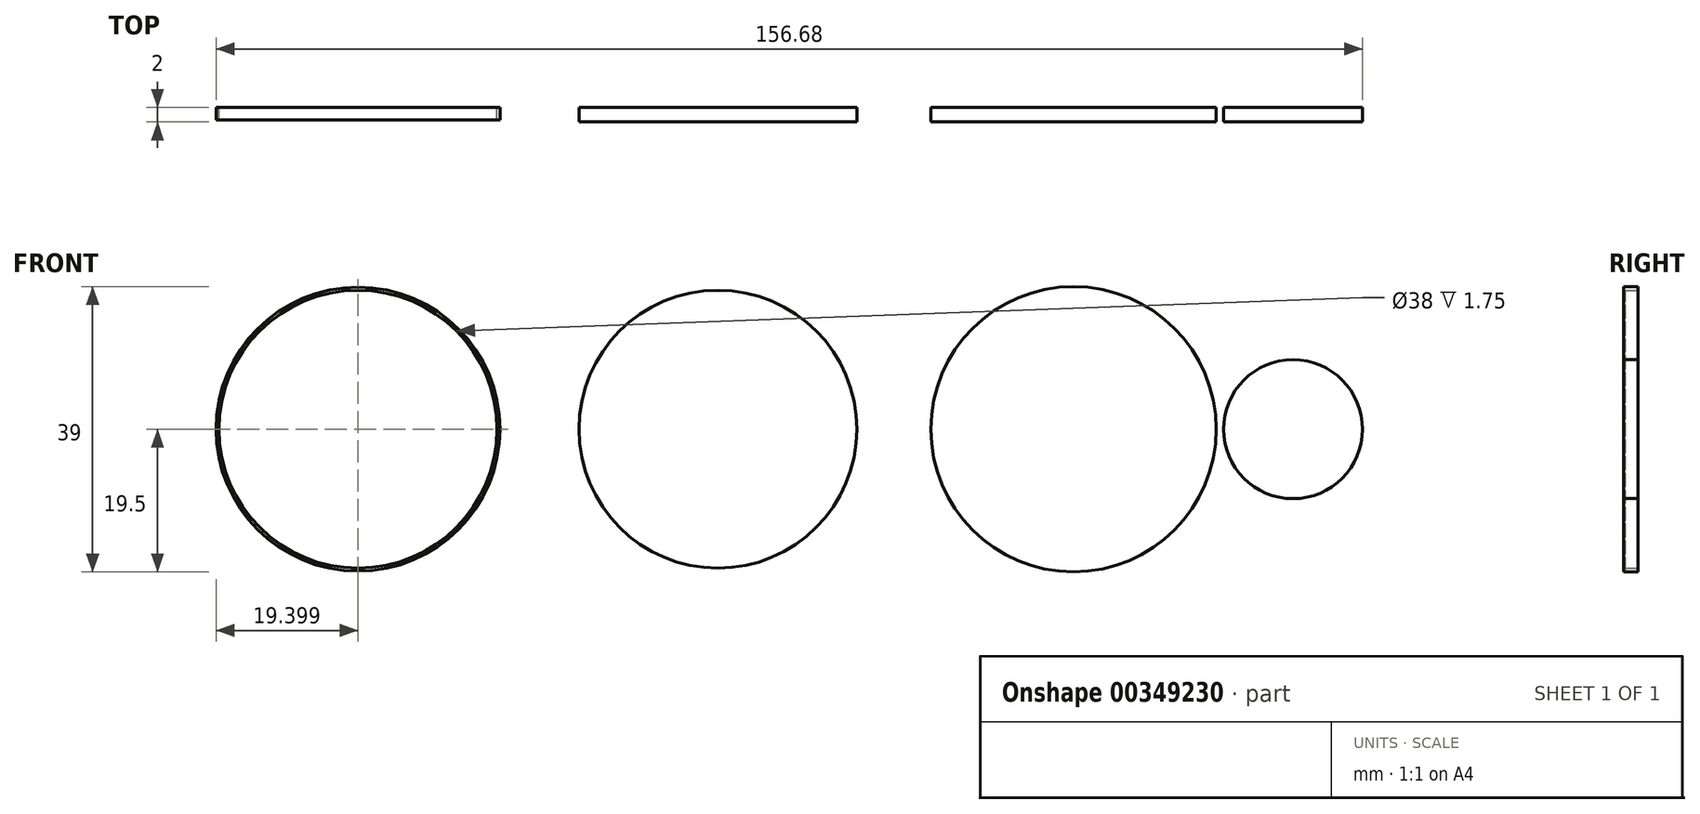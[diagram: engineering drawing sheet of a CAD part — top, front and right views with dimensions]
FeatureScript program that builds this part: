
annotation { "Feature Type Name" : "Feature", "Feature Type Description" : "" }
export const myFeature = defineFeature(function(context is Context, id is Id, definition is map)
    precondition{}
    {
        {
            var Q0;
            Q0=qCreatedBy(makeId("Front.planeOp"),FACE);
            var sketch = newSketch(context, id + "F0", { "sketchPlane" : qUnion([Q0])});
            skCircle(sketch, "E0", {"center": v(0, 0) * mm, "radius": 19.5 * mm});
            skLineSegment(sketch, "E1", {"start": v(0, 0) * mm, "end": v(30, 0) * mm});
            skCircle(sketch, "E2", {"center": v(30, 0) * mm, "radius": 9.5 * mm});
            skCircle(sketch, "E3", {"center": v(-48.6, 0) * mm, "radius": 19 * mm});
            skCircle(sketch, "E4", {"center": v(-97.78, 0) * mm, "radius": 19.4 * mm});
            skCircle(sketch, "E5", {"center": v(-97.78, 0) * mm, "radius": 19 * mm});
            skSolve(sketch);
        }
        {
            var Q0;
            Q0=makeQuery(id+"F0.imprint","IMPRINT",FACE,{"disambiguationData":[TD([[makeQuery(id+"F0.imprint","IMPRINT",EDGE,{"derivedFrom":sQuery(id+"F0.wireOp",EDGE,"E0")}),1.0]])]});
            var Q1;
            Q1=makeQuery(id+"F0.imprint","IMPRINT",FACE,{"disambiguationData":[TD([[makeQuery(id+"F0.imprint","IMPRINT",EDGE,{"derivedFrom":sQuery(id+"F0.wireOp",EDGE,"E2")}),1.0]])]});
            var Q2;
            Q2=makeQuery(id+"F0.imprint","IMPRINT",FACE,{"disambiguationData":[TD([[makeQuery(id+"F0.imprint","IMPRINT",EDGE,{"derivedFrom":sQuery(id+"F0.wireOp",EDGE,"E3")}),1.0]])]});
            extrude(context, id + "F1", {"entities" : qUnion([Q0, Q1, Q2]), "depth" : 2 * mm});
        }
        {
            var Q0;
            Q0=makeQuery(id+"F0.imprint","IMPRINT",FACE,{"disambiguationData":[TD([[makeQuery(id+"F0.imprint","IMPRINT",EDGE,{"derivedFrom":sQuery(id+"F0.wireOp",EDGE,"E4")}),1.0]])]});
            extrude(context, id + "F2", {"entities" : qUnion([Q0]), "depth" : 1.75 * mm});
        }
    });
